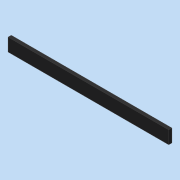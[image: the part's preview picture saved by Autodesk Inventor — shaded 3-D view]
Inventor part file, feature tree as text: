
AUTODESK INVENTOR PART (.ipt)
format: ipt  version: 2020 (Build 240168000, 168)  size: 78,336 bytes
history: native  units: mm
features: other x1, extrude x1
ambient origin geometry x8: Origin, YZ Plane, XZ Plane, XY Plane, X Axis, Y Axis, Z Axis, Center Point
bodies: Body1 (feature_tree)
feature tree (2):
  other  "實體1"
  extrude  "擠出1"  Depth=10.0mm
